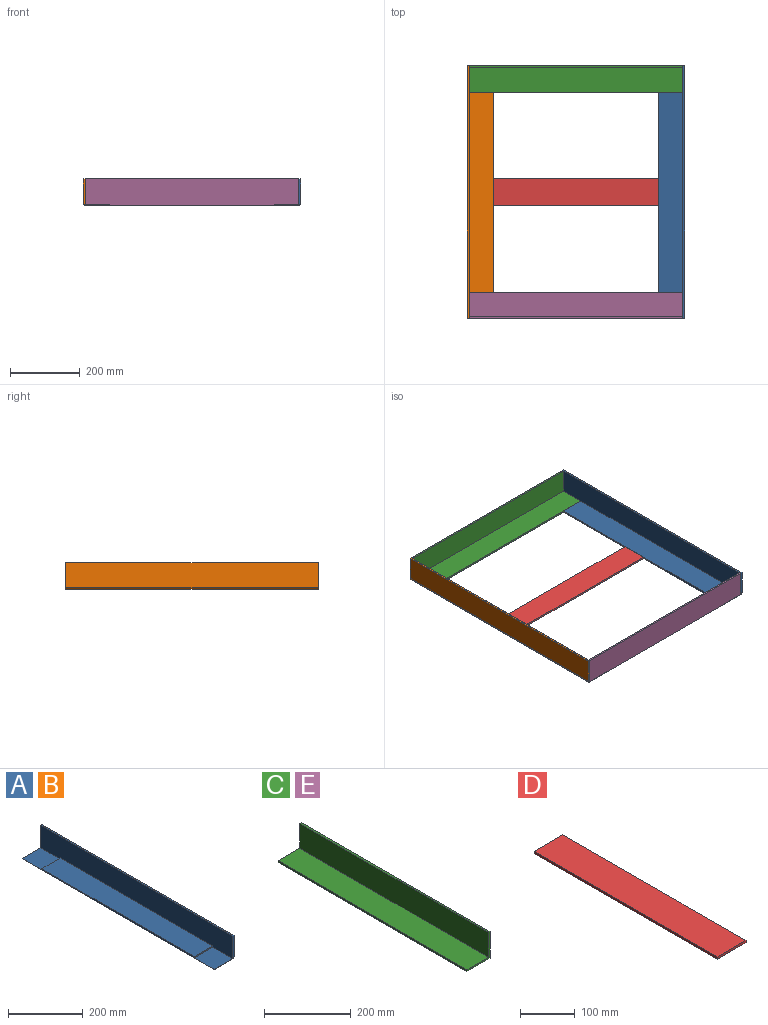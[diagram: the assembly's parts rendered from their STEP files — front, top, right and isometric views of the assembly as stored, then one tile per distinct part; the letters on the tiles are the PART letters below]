
ASSEMBLY  parts=5 mates=4
PART A: 13 faces, bbox 75x725x75 mm
  f0: plane 575x70mm, normal (0,0,1), area 40250mm2, adj f1,f3,f9,f11
  f1: plane 725x5mm, normal (-1,0,0), area 3025mm2, adj f0,f2,f4,f7,f9,f10,f11,f12
  f2: plane 75x75mm, normal (0,-1,0), area 439.6mm2, adj f1,f3,f4,f5,f6,f8,f12
  f3: plane 725x74mm, normal (-1,0,0), area 51350mm2, adj f0,f2,f6,f7,f9,f10,f11,f12
  f4: plane 725x70mm, normal (0,0,-1), area 50750mm2, adj f1,f2,f7,f8
  f5: plane 725x70mm, normal (1,0,0), area 50750mm2, adj f2,f6,f7,f8
  f6: plane 725x5mm, normal (0,0,1), area 3625mm2, adj f2,f3,f5,f7
  f7: plane 75x75mm, normal (0,1,0), area 439.6mm2, adj f1,f3,f4,f5,f6,f8,f10
  f8: cylinder r=5mm len=725mm, axis (0,-1,0), area 5694.1mm2, adj f2,f4,f5,f7
  f9: plane 70x4mm, normal (0,1,0), area 280mm2, adj f0,f1,f3,f10
  f10: plane 75x70mm, normal (0,0,1), area 5250mm2, adj f1,f3,f7,f9
  f11: plane 70x4mm, normal (0,-1,0), area 280mm2, adj f0,f1,f3,f12
  f12: plane 75x70mm, normal (0,0,1), area 5250mm2, adj f1,f2,f3,f11
PART B: same geometry as A
PART C: 8 faces, bbox 75x615x75 mm
  f0: plane 615x70mm, normal (-1,0,0), area 43050mm2, adj f1,f5,f6,f7
  f1: plane 615x70mm, normal (0,0,1), area 43050mm2, adj f0,f2,f6,f7
  f2: plane 615x5mm, normal (-1,0,0), area 3075mm2, adj f1,f3,f6,f7
  f3: plane 615x75mm, normal (0,0,-1), area 46125mm2, adj f2,f4,f6,f7
  f4: plane 615x75mm, normal (1,0,0), area 46125mm2, adj f3,f5,f6,f7
  f5: plane 615x5mm, normal (0,0,1), area 3075mm2, adj f0,f4,f6,f7
  f6: plane 75x75mm, normal (0,-1,0), area 725mm2, adj f0,f1,f2,f3,f4,f5
  f7: plane 75x75mm, normal (0,1,0), area 725mm2, adj f0,f1,f2,f3,f4,f5
PART D: 6 faces, bbox 75x475x5 mm
  f0: plane 475x75mm, normal (0,0,-1), area 35625mm2, adj f1,f3,f4,f5
  f1: plane 475x5mm, normal (1,0,0), area 2375mm2, adj f0,f2,f4,f5
  f2: plane 475x75mm, normal (0,0,1), area 35625mm2, adj f1,f3,f4,f5
  f3: plane 475x5mm, normal (-1,0,0), area 2375mm2, adj f0,f2,f4,f5
  f4: plane 75x5mm, normal (0,-1,0), area 375mm2, adj f0,f1,f2,f3
  f5: plane 75x5mm, normal (0,1,0), area 375mm2, adj f0,f1,f2,f3
PART E: same geometry as C
PLACE A t=(112.46,60.22,71.92)mm
PLACE B rot(axis=(0,0,1),180deg) t=(-512.54,-664.78,71.92)mm
PLACE C rot(axis=(0,0,1),90deg) t=(-507.54,60.22,71.92)mm
PLACE D rot(axis=(0,0,1),90deg) t=(-437.54,-302.28,74.32)mm
PLACE E rot(axis=(0,0,-1),90deg) t=(107.46,-664.78,71.92)mm
MATE fastened C.f6 <-> A.f3  axis (1,0,0) through (107.46,60.22,146.92)mm
MATE fastened D.f5 <-> B.f1  axis (-1,0,0) through (-437.54,-302.28,74.32)mm
MATE fastened E.f7 <-> A.f3  axis (1,0,0) through (107.46,-664.78,146.92)mm
MATE fastened B.f3 <-> E.f6  axis (1,0,0) through (-507.54,-664.78,146.92)mm
